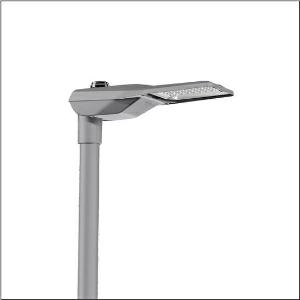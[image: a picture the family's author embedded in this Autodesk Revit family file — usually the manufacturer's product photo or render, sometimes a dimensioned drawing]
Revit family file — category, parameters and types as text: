
# Revit family: streetlight_sl_21_mini___st1_0a_5xe6d27n08hb_8446
name_source: partatom
category: Lighting Fixtures
units: mm (PartAtom-declared; Revit-internal decimal feet)

## family parameters
Cut with Voids When Loaded = No
Host = Face
Light Source = No
Part Type = Normal
Room Calculation Point = No
Round Connector Dimension = Use Diameter
Shared = No

## types (1)
- --- (1 x LED, 7490 lm, 66 W, 2200K)
    Apparent Load = 66 VA
    CIE Flux Codes = 37 72 97 100 100
    Color Rendering = 70
    Color Temperature = 2200K
    Default Elevation = 1800 mm
    Description = Streetlight SL 21 mini, mast luminaire, primary light control with lens, of PMMA, primary optical cover: cover, of toughened safety glass, transparent, light distribution: ST1.0a, light emission: direct distribution, primary light characteristic: asymmetric, installation type: side-entry, LED, 3G 1.5mm², High Power LED, rated luminous flux: 7.490lm, luminous efficacy: 114lm/W, light colour: 722, colour temperature: 2200K, control: overheat protection, pre-setting: linear dimming characteristic, constant luminous flux control, time-dependent luminous flux control, flexible luminous flux parameterisation, mains connection: 230..240V, AC, 50/60Hz, connection cable pre-assembled, cable length: 8,5m, wiring characteristics: H07RN-F, start of lifetime: 66W, end of service life: 69W, reduction: 30W, luminaire housing, of diecast aluminium (EN AC-44300), powder-coated, Siteco® metallic grey (DB 702S), corrosivity category C5 mid according to DIN EN ISO 12944, multi-level sealing system, sealing non-destructively replaceable, inclination adjustable: 0°, 5°, 10°, 15°, length: 628mm, width: 235mm, height: 110mm, spigot size: 42mm (side-entry), protection rating (complete): IP66, insulation class (complete): insulation class I (protective earthing), certification: CE, ENEC, ENEC+, VDE, impact resistance: IK09, permissible operating ambient temperature for outdoor applications: -40..+50°C, standard-compliant lighting for roads and squares, packaging unit: 1 piece

Light Distribution: ST1.0a
    Height = 110 mm
    Lamp = 1 x LED
    Lamp Light Flux = 7490 lm
    Lamp Power = 66 W
    Lamp count = 1
    Length = 625 mm
    Luminous efficacy = 113 lm/W
    Manufacturer = Siteco
    ModVariant = No
    Model = 5XE6D27N08HB
    Number of Poles = 1
    OnlyDefault = Yes
    Power Factor = 1
    Product Name = Streetlight SL 21 mini | ST1.0a
    Product group = mast luminaire | pylon top
    ProductGroupID = 6100
    Protection Class = Protection class I
    Protection Degree = IP 66
    RLX_Detail_Level = 1
    RLX_Emergency_Light_Flux = 0 lm
    RLX_Emergency_Type = 0
    RLX_Emergency_Type_DB = No
    RlxData = <blob elided: 93629 chars, md5=92bebf5b>
    Socket = socket
    Standby Power = 0 W
    System Light Flux = 7490 lm
    System Power = 66 W
    Type Comments = factory setting: luminous flux: 100 % | dim-lin: 254 | 670 mA
    Type Image = l_1294379.jpg
    URL = http://relux.com
    VarID = @adj_106163
    Voltage = 0 V
    Weight = 0.00 kg
    Width = 234 mm

## geometry (parser evidence)
native form markers: Blend x4, Sweep x10
no freeform markers — native parametric forms only
